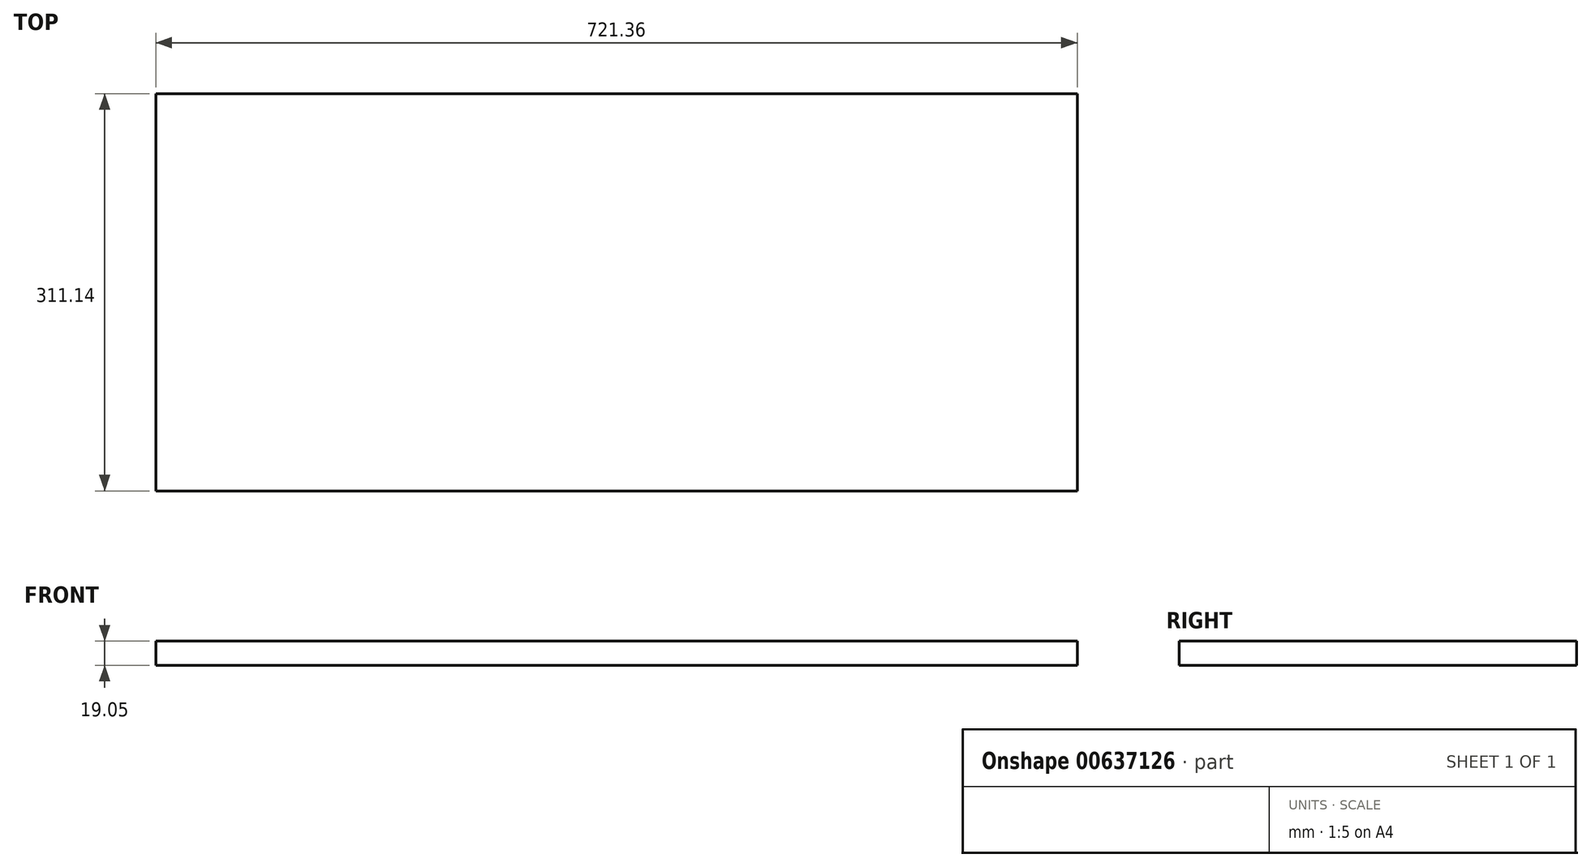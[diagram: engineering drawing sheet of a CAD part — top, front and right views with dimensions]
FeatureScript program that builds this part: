
annotation { "Feature Type Name" : "Feature", "Feature Type Description" : "" }
export const myFeature = defineFeature(function(context is Context, id is Id, definition is map)
    precondition{}
    {
        {
            var Q0;
            Q0=qCreatedBy(makeId("Top.planeOp"),FACE);
            var sketch = newSketch(context, id + "F0", { "sketchPlane" : qUnion([Q0])});
            skLineSegment(sketch, "E0.bottom", {"start": v(-360.68, 155.58) * mm, "end": v(360.68, 155.58) * mm});
            skLineSegment(sketch, "E0.top", {"start": v(-360.68, -155.58) * mm, "end": v(360.68, -155.58) * mm});
            skLineSegment(sketch, "E0.left", {"start": v(-360.68, 155.58) * mm, "end": v(-360.68, -155.58) * mm});
            skLineSegment(sketch, "E0.right", {"start": v(360.68, 155.57) * mm, "end": v(360.68, -155.58) * mm});
            skPoint(sketch, "E0.middle", {"position": v(0, 0) * mm});
            skSolve(sketch);
        }
        {
            var Q0;
            Q0=makeQuery(id+"F0.imprint","IMPRINT",FACE,{"disambiguationData":[TD([[makeQuery(id+"F0.imprint","IMPRINT",EDGE,{"derivedFrom":sQuery(id+"F0.wireOp",EDGE,"E0.bottom")}),-1.0]])]});
            extrude(context, id + "F1", {"entities" : qUnion([Q0]), "depth" : 19.05 * mm, "offsetDistance" : 25.4 * mm});
        }
    });
